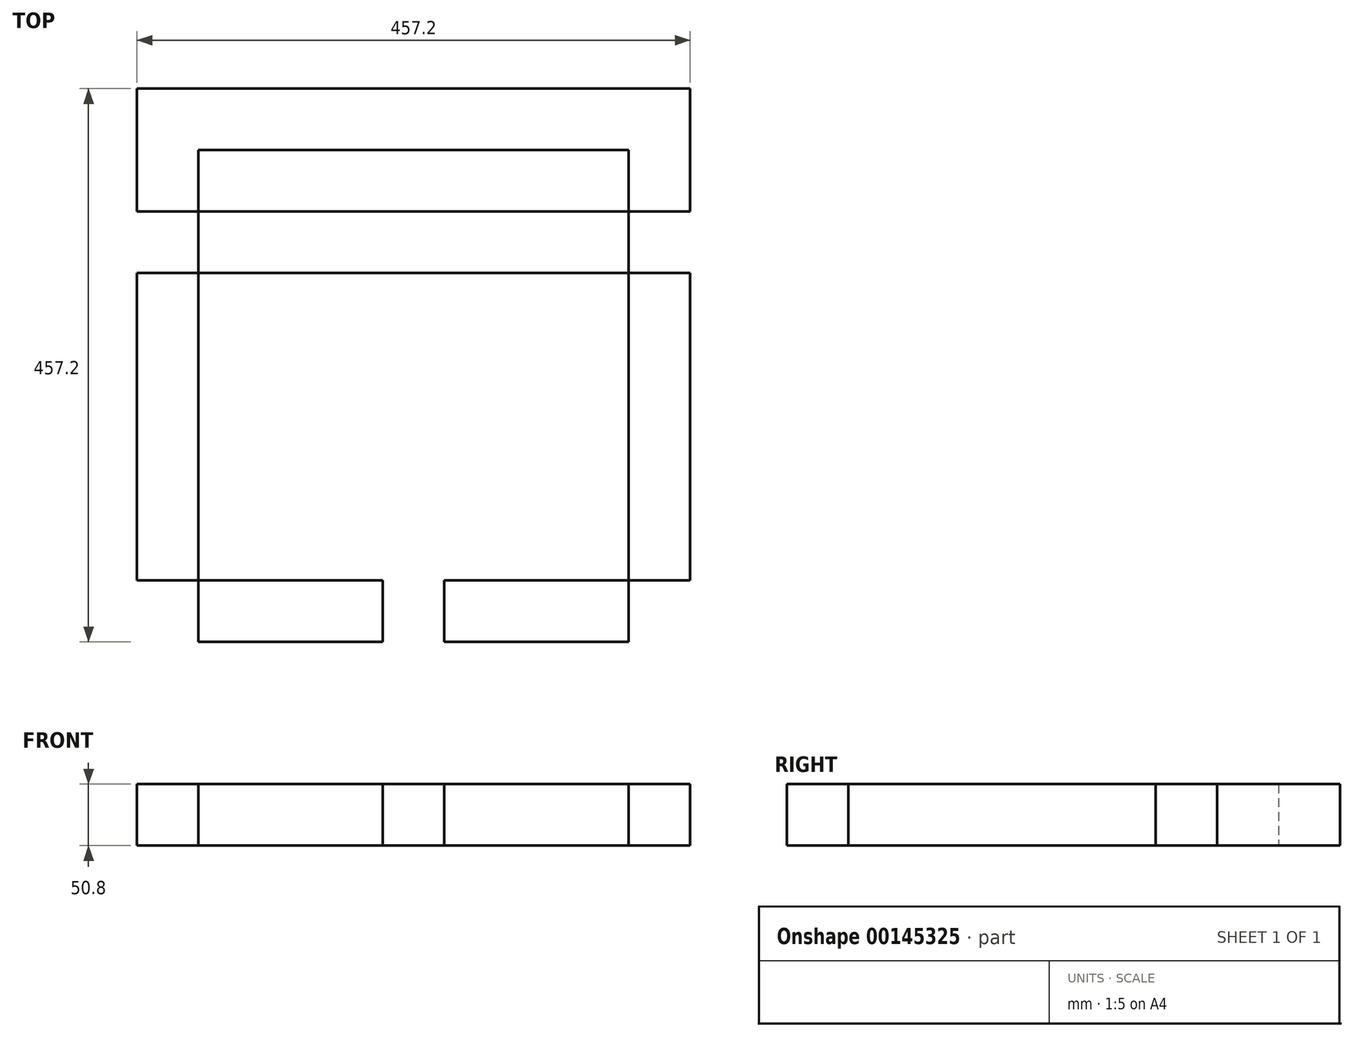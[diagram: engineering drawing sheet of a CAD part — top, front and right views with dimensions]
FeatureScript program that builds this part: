
annotation { "Feature Type Name" : "Feature", "Feature Type Description" : "" }
export const myFeature = defineFeature(function(context is Context, id is Id, definition is map)
    precondition{}
    {
        {
            var Q0;
            Q0=qCreatedBy(makeId("Top.planeOp"),FACE);
            var sketch = newSketch(context, id + "F0", { "sketchPlane" : qUnion([Q0])});
            skLineSegment(sketch, "E0.bottom", {"start": v(-254, 124.27) * mm, "end": v(203.2, 124.27) * mm});
            skLineSegment(sketch, "E0.top", {"start": v(-254, 73.47) * mm, "end": v(203.2, 73.47) * mm});
            skLineSegment(sketch, "E0.left", {"start": v(-254, 124.27) * mm, "end": v(-254, 73.47) * mm});
            skLineSegment(sketch, "E0.right", {"start": v(203.2, 124.27) * mm, "end": v(203.2, 73.47) * mm});
            skLineSegment(sketch, "E1.bottom", {"start": v(-254, 124.27) * mm, "end": v(-203.2, 124.27) * mm});
            skLineSegment(sketch, "E1.top", {"start": v(-254, -332.93) * mm, "end": v(-203.2, -332.93) * mm});
            skLineSegment(sketch, "E1.left", {"start": v(-254, 124.27) * mm, "end": v(-254, -332.93) * mm});
            skLineSegment(sketch, "E1.right", {"start": v(-203.2, 124.27) * mm, "end": v(-203.2, -332.93) * mm});
            skLineSegment(sketch, "E2.bottom", {"start": v(203.2, 124.27) * mm, "end": v(152.4, 124.27) * mm});
            skLineSegment(sketch, "E2.top", {"start": v(203.2, -332.93) * mm, "end": v(152.4, -332.93) * mm});
            skLineSegment(sketch, "E2.left", {"start": v(203.2, 124.27) * mm, "end": v(203.2, -332.93) * mm});
            skLineSegment(sketch, "E2.right", {"start": v(152.4, 124.27) * mm, "end": v(152.4, -332.93) * mm});
            skLineSegment(sketch, "E3.bottom", {"start": v(203.2, -332.93) * mm, "end": v(0, -332.93) * mm});
            skLineSegment(sketch, "E3.top", {"start": v(203.2, -282.13) * mm, "end": v(0, -282.13) * mm});
            skLineSegment(sketch, "E3.left", {"start": v(203.2, -332.93) * mm, "end": v(203.2, -282.13) * mm});
            skLineSegment(sketch, "E3.right", {"start": v(0, -332.93) * mm, "end": v(0, -282.13) * mm});
            skLineSegment(sketch, "E4.bottom", {"start": v(-254, -332.93) * mm, "end": v(-50.8, -332.93) * mm});
            skLineSegment(sketch, "E4.top", {"start": v(-254, -282.13) * mm, "end": v(-50.8, -282.13) * mm});
            skLineSegment(sketch, "E4.left", {"start": v(-254, -332.93) * mm, "end": v(-254, -282.13) * mm});
            skLineSegment(sketch, "E4.right", {"start": v(-50.8, -332.93) * mm, "end": v(-50.8, -282.13) * mm});
            skLineSegment(sketch, "E5.bottom", {"start": v(-254, 22.67) * mm, "end": v(203.2, 22.67) * mm});
            skLineSegment(sketch, "E5.top", {"start": v(-254, -28.13) * mm, "end": v(203.2, -28.13) * mm});
            skLineSegment(sketch, "E5.left", {"start": v(-254, 22.67) * mm, "end": v(-254, -28.13) * mm});
            skLineSegment(sketch, "E5.right", {"start": v(203.2, 22.67) * mm, "end": v(203.2, -28.13) * mm});
            skSolve(sketch);
        }
        {
            var Q0;
            {var subQ5=sQuery(id+"F0.wireOp",EDGE,"E3.right");Q0=makeQuery(id+"F0.imprint","IMPRINT",FACE,{"disambiguationData":[TD([[makeQuery(id+"F0.imprint","IMPRINT",EDGE,{"derivedFrom":subQ5}),-1.0]])]});}
            var Q1;
            {var subQ5=sQuery(id+"F0.wireOp",EDGE,"E3.left");Q1=makeQuery(id+"F0.imprint","IMPRINT",FACE,{"disambiguationData":[TD([[makeQuery(id+"F0.imprint","IMPRINT",EDGE,{"derivedFrom":subQ5}),1.0]])]});}
            var Q2;
            {var subQ3=sQuery(id+"F0.wireOp",EDGE,"E5.top");var subQ5=sQuery(id+"F0.wireOp",EDGE,"E2.right");var subQ6=makeQuery(id+"F0.imprint","INTERSECT",VERTEX,{"derivedFrom":[subQ5,subQ3]});Q2=makeQuery(id+"F0.imprint","IMPRINT",FACE,{"disambiguationData":[TD([[makeQuery(id+"F0.imprint","IMPRINT",EDGE,{"disambiguationData":[TD([[subQ6,-1.0]])],"derivedFrom":subQ5}),1.0]])]});}
            var Q3;
            {var subQ5=sQuery(id+"F0.wireOp",EDGE,"E4.right");Q3=makeQuery(id+"F0.imprint","IMPRINT",FACE,{"disambiguationData":[TD([[makeQuery(id+"F0.imprint","IMPRINT",EDGE,{"derivedFrom":subQ5}),1.0]])]});}
            var Q4;
            {var subQ5=sQuery(id+"F0.wireOp",EDGE,"E4.left");Q4=makeQuery(id+"F0.imprint","IMPRINT",FACE,{"disambiguationData":[TD([[makeQuery(id+"F0.imprint","IMPRINT",EDGE,{"derivedFrom":subQ5}),-1.0]])]});}
            var Q5;
            {var subQ3=sQuery(id+"F0.wireOp",EDGE,"E5.top");var subQ5=sQuery(id+"F0.wireOp",EDGE,"E1.right");var subQ6=makeQuery(id+"F0.imprint","INTERSECT",VERTEX,{"derivedFrom":[subQ5,subQ3]});Q5=makeQuery(id+"F0.imprint","IMPRINT",FACE,{"disambiguationData":[TD([[makeQuery(id+"F0.imprint","IMPRINT",EDGE,{"disambiguationData":[TD([[subQ6,-1.0]])],"derivedFrom":subQ5}),-1.0]])]});}
            var Q6;
            {var subQ5=sQuery(id+"F0.wireOp",EDGE,"E5.left");Q6=makeQuery(id+"F0.imprint","IMPRINT",FACE,{"disambiguationData":[TD([[makeQuery(id+"F0.imprint","IMPRINT",EDGE,{"derivedFrom":subQ5}),1.0]])]});}
            var Q7;
            {var subQ0=sQuery(id+"F0.wireOp",EDGE,"E5.top");var subQ1=sQuery(id+"F0.wireOp",EDGE,"E1.right");var subQ2=makeQuery(id+"F0.imprint","INTERSECT",VERTEX,{"derivedFrom":[subQ1,subQ0]});Q7=makeQuery(id+"F0.imprint","IMPRINT",FACE,{"disambiguationData":[TD([[makeQuery(id+"F0.imprint","IMPRINT",EDGE,{"disambiguationData":[TD([[subQ2,1.0]])],"derivedFrom":subQ1}),1.0]])]});}
            var Q8;
            {var subQ5=sQuery(id+"F0.wireOp",EDGE,"E5.right");Q8=makeQuery(id+"F0.imprint","IMPRINT",FACE,{"disambiguationData":[TD([[makeQuery(id+"F0.imprint","IMPRINT",EDGE,{"derivedFrom":subQ5}),-1.0]])]});}
            var Q9;
            {var subQ0=sQuery(id+"F0.wireOp",EDGE,"E2.left");var subQ1=sQuery(id+"F0.wireOp",EDGE,"E0.top");var subQ2=makeQuery(id+"F0.imprint","INTERSECT",VERTEX,{"derivedFrom":[subQ1,subQ0]});Q9=makeQuery(id+"F0.imprint","IMPRINT",FACE,{"disambiguationData":[TD([[makeQuery(id+"F0.imprint","IMPRINT",EDGE,{"disambiguationData":[TD([[subQ2,1.0]])],"derivedFrom":subQ1}),-1.0]])]});}
            var Q10;
            {var subQ5=sQuery(id+"F0.wireOp",EDGE,"E2.bottom");Q10=makeQuery(id+"F0.imprint","IMPRINT",FACE,{"disambiguationData":[TD([[makeQuery(id+"F0.imprint","IMPRINT",EDGE,{"derivedFrom":subQ5}),1.0]])]});}
            var Q11;
            {var subQ0=sQuery(id+"F0.wireOp",EDGE,"E0.bottom");Q11=makeQuery(id+"F0.imprint","IMPRINT",FACE,{"disambiguationData":[TD([[makeQuery(id+"F0.imprint","IMPRINT",EDGE,{"derivedFrom":subQ0}),-1.0]])]});}
            var Q12;
            {var subQ5=sQuery(id+"F0.wireOp",EDGE,"E1.bottom");Q12=makeQuery(id+"F0.imprint","IMPRINT",FACE,{"disambiguationData":[TD([[makeQuery(id+"F0.imprint","IMPRINT",EDGE,{"derivedFrom":subQ5}),-1.0]])]});}
            var Q13;
            {var subQ0=sQuery(id+"F0.wireOp",EDGE,"E1.left");var subQ1=sQuery(id+"F0.wireOp",EDGE,"E0.top");var subQ2=makeQuery(id+"F0.imprint","INTERSECT",VERTEX,{"derivedFrom":[subQ1,subQ0]});Q13=makeQuery(id+"F0.imprint","IMPRINT",FACE,{"disambiguationData":[TD([[makeQuery(id+"F0.imprint","IMPRINT",EDGE,{"disambiguationData":[TD([[subQ2,-1.0]])],"derivedFrom":subQ1}),-1.0]])]});}
            extrude(context, id + "F1", {"entities" : qUnion([Q0, Q1, Q2, Q3, Q4, Q5, Q6, Q7, Q8, Q9, Q10, Q11, Q12, Q13]), "depth" : 50.8 * mm});
        }
    });
